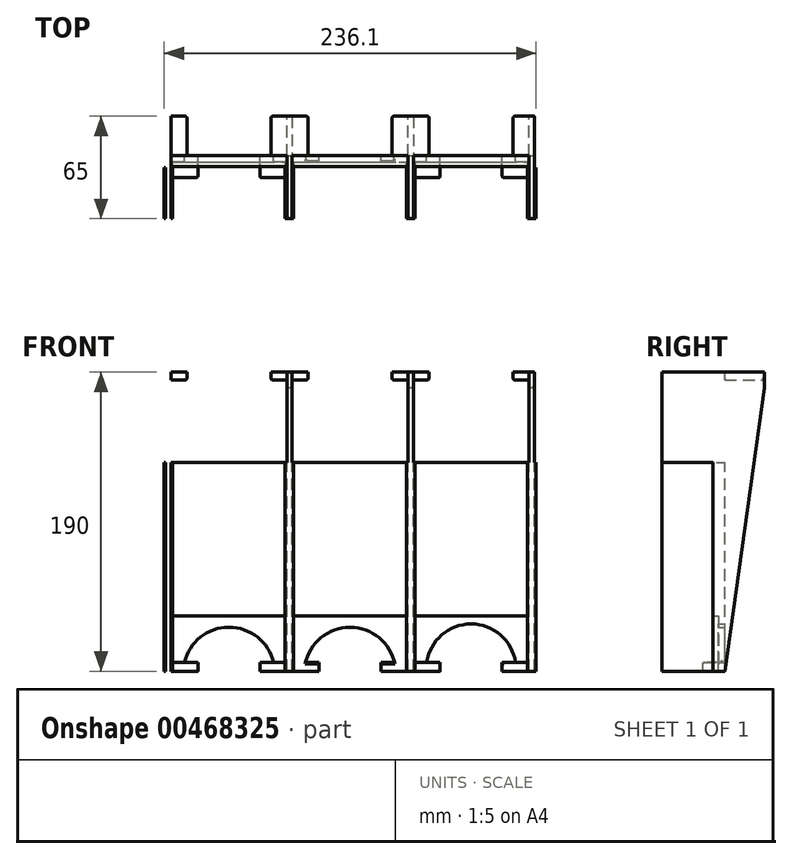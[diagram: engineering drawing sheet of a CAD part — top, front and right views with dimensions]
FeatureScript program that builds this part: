
annotation { "Feature Type Name" : "Feature", "Feature Type Description" : "" }
export const myFeature = defineFeature(function(context is Context, id is Id, definition is map)
    precondition{}
    {
        {
            var Q0;
            Q0=qCreatedBy(makeId("Top.planeOp"),FACE);
            var sketch = newSketch(context, id + "F0", { "sketchPlane" : qUnion([Q0])});
            skLineSegment(sketch, "E0.bottom", {"start": v(118.05, -35) * mm, "end": v(-118.05, -35) * mm});
            skLineSegment(sketch, "E0.top", {"start": v(118.05, 35) * mm, "end": v(-118.05, 35) * mm});
            skLineSegment(sketch, "E0.left", {"start": v(118.05, -35) * mm, "end": v(118.05, 35) * mm});
            skLineSegment(sketch, "E0.right", {"start": v(-118.05, -35) * mm, "end": v(-118.05, 35) * mm});
            skPoint(sketch, "E0.middle", {"position": v(0, 0) * mm});
            skLineSegment(sketch, "E1", {"start": v(-118.05, 30) * mm, "end": v(118.05, 30) * mm});
            skLineSegment(sketch, "E2", {"start": v(-112.65, -35) * mm, "end": v(-112.65, -2.5) * mm});
            skLineSegment(sketch, "E3", {"start": v(-112.65, -2.5) * mm, "end": v(-113.65, -2.5) * mm});
            skLineSegment(sketch, "E4", {"start": v(-113.65, -2.5) * mm, "end": v(-113.65, 30) * mm});
            skLineSegment(sketch, "E5", {"start": v(-41.15, -2.5) * mm, "end": v(-40.15, -2.5) * mm});
            skLineSegment(sketch, "E6", {"start": v(-40.15, -2.5) * mm, "end": v(-40.15, 30) * mm});
            skLineSegment(sketch, "E7", {"start": v(-41.15, -2.5) * mm, "end": v(-41.15, -35) * mm});
            skLineSegment(sketch, "E8", {"start": v(-36.75, 30) * mm, "end": v(-36.75, -2.5) * mm});
            skLineSegment(sketch, "E9", {"start": v(-36.75, -2.5) * mm, "end": v(-35.75, -2.5) * mm});
            skLineSegment(sketch, "E10", {"start": v(-35.75, -2.5) * mm, "end": v(-35.75, -35) * mm});
            skLineSegment(sketch, "E11", {"start": v(36.75, 30) * mm, "end": v(36.75, -2.5) * mm});
            skLineSegment(sketch, "E12", {"start": v(36.75, -2.5) * mm, "end": v(35.75, -2.5) * mm});
            skLineSegment(sketch, "E13", {"start": v(35.75, -2.5) * mm, "end": v(35.75, -35) * mm});
            skLineSegment(sketch, "E14", {"start": v(40.15, 30) * mm, "end": v(40.15, -2.5) * mm});
            skLineSegment(sketch, "E15", {"start": v(40.15, -2.5) * mm, "end": v(41.15, -2.5) * mm});
            skLineSegment(sketch, "E16", {"start": v(41.15, -2.5) * mm, "end": v(41.15, -35) * mm});
            skLineSegment(sketch, "E17", {"start": v(113.65, 30) * mm, "end": v(113.65, -2.5) * mm});
            skLineSegment(sketch, "E18", {"start": v(113.65, -2.5) * mm, "end": v(112.65, -2.5) * mm});
            skLineSegment(sketch, "E19", {"start": v(112.65, -2.5) * mm, "end": v(112.65, -35) * mm});
            skLineSegment(sketch, "E20", {"start": v(-113.65, -2) * mm, "end": v(-40.15, -2) * mm});
            skLineSegment(sketch, "E21", {"start": v(-36.75, -2) * mm, "end": v(36.75, -2) * mm});
            skLineSegment(sketch, "E22", {"start": v(40.15, -2) * mm, "end": v(113.65, -2) * mm});
            skLineSegment(sketch, "E23", {"start": v(-112.65, -2.5) * mm, "end": v(-112.65, -2) * mm});
            skLineSegment(sketch, "E24", {"start": v(-41.15, -2.5) * mm, "end": v(-41.15, -2) * mm});
            skLineSegment(sketch, "E25", {"start": v(-35.75, -2.5) * mm, "end": v(-35.75, -2) * mm});
            skLineSegment(sketch, "E26", {"start": v(35.75, -2.5) * mm, "end": v(35.75, -2) * mm});
            skLineSegment(sketch, "E27", {"start": v(41.15, -2.5) * mm, "end": v(41.15, -2) * mm});
            skLineSegment(sketch, "E28", {"start": v(112.65, -2.5) * mm, "end": v(112.65, -2) * mm});
            skLineSegment(sketch, "E29", {"start": v(-118.05, -2.5) * mm, "end": v(-117.05, -2.5) * mm});
            skLineSegment(sketch, "E30", {"start": v(-117.05, -2.5) * mm, "end": v(-117.05, 35) * mm});
            skLineSegment(sketch, "E31", {"start": v(118.05, -2.5) * mm, "end": v(117.05, -2.5) * mm});
            skLineSegment(sketch, "E32", {"start": v(117.05, -2.5) * mm, "end": v(117.05, 30) * mm});
            skLineSegment(sketch, "E33", {"start": v(-113.65, 5) * mm, "end": v(-103.65, 5) * mm});
            skLineSegment(sketch, "E34", {"start": v(-103.65, 5) * mm, "end": v(-103.65, 30) * mm});
            skLineSegment(sketch, "E35", {"start": v(-40.15, 5) * mm, "end": v(-50.15, 5) * mm});
            skLineSegment(sketch, "E36", {"start": v(-50.15, 5) * mm, "end": v(-50.15, 30) * mm});
            skLineSegment(sketch, "E37", {"start": v(-36.75, 5) * mm, "end": v(-26.75, 5) * mm});
            skLineSegment(sketch, "E38", {"start": v(-26.75, 5) * mm, "end": v(-26.75, 30) * mm});
            skLineSegment(sketch, "E39", {"start": v(36.75, 5) * mm, "end": v(26.75, 5) * mm});
            skLineSegment(sketch, "E40", {"start": v(26.75, 5) * mm, "end": v(26.75, 30) * mm});
            skLineSegment(sketch, "E41", {"start": v(40.15, 5) * mm, "end": v(50.15, 5) * mm});
            skLineSegment(sketch, "E42", {"start": v(50.15, 5) * mm, "end": v(50.15, 30) * mm});
            skLineSegment(sketch, "E43", {"start": v(113.65, 5) * mm, "end": v(103.65, 5) * mm});
            skLineSegment(sketch, "E44", {"start": v(103.65, 5) * mm, "end": v(103.65, 30) * mm});
            skLineSegment(sketch, "E45", {"start": v(117.05, 30) * mm, "end": v(117.05, 35) * mm});
            skLineSegment(sketch, "E46.bottom", {"start": v(-117.05, -2.5) * mm, "end": v(-113.65, -2.5) * mm, "construction": true});
            skLineSegment(sketch, "E46.top", {"start": v(-117.05, -35) * mm, "end": v(-113.65, -35) * mm});
            skLineSegment(sketch, "E46.left", {"start": v(-117.05, -2.5) * mm, "end": v(-117.05, -35) * mm});
            skLineSegment(sketch, "E46.right", {"start": v(-113.65, -2.5) * mm, "end": v(-113.65, -35) * mm});
            skLineSegment(sketch, "E47.bottom", {"start": v(-40.15, -2.5) * mm, "end": v(-36.75, -2.5) * mm, "construction": true});
            skLineSegment(sketch, "E47.top", {"start": v(-40.15, -35) * mm, "end": v(-36.75, -35) * mm, "construction": true});
            skLineSegment(sketch, "E47.left", {"start": v(-40.15, -2.5) * mm, "end": v(-40.15, -35) * mm});
            skLineSegment(sketch, "E47.right", {"start": v(-36.75, -2.5) * mm, "end": v(-36.75, -35) * mm});
            skLineSegment(sketch, "E48.bottom", {"start": v(36.75, -2.5) * mm, "end": v(40.15, -2.5) * mm});
            skLineSegment(sketch, "E48.top", {"start": v(36.75, -35) * mm, "end": v(40.15, -35) * mm});
            skLineSegment(sketch, "E48.left", {"start": v(36.75, -2.5) * mm, "end": v(36.75, -35) * mm});
            skLineSegment(sketch, "E48.right", {"start": v(40.15, -2.5) * mm, "end": v(40.15, -35) * mm});
            skLineSegment(sketch, "E49.bottom", {"start": v(113.65, -2.5) * mm, "end": v(117.05, -2.5) * mm});
            skLineSegment(sketch, "E49.top", {"start": v(113.65, -35) * mm, "end": v(117.05, -35) * mm});
            skLineSegment(sketch, "E49.left", {"start": v(113.65, -2.5) * mm, "end": v(113.65, -35) * mm});
            skLineSegment(sketch, "E49.right", {"start": v(117.05, -2.5) * mm, "end": v(117.05, -35) * mm});
            skLineSegment(sketch, "E50", {"start": v(-103.65, 5) * mm, "end": v(-50.15, 5) * mm});
            skLineSegment(sketch, "E51", {"start": v(-26.75, 5) * mm, "end": v(26.75, 5) * mm});
            skLineSegment(sketch, "E52", {"start": v(50.15, 5) * mm, "end": v(103.65, 5) * mm});
            skSolve(sketch);
        }
        {
            var Q0;
            {var subQ13=sQuery(id+"F0.wireOp",EDGE,"E5");Q0=makeQuery(id+"F0.imprint","IMPRINT",FACE,{"disambiguationData":[TD([[makeQuery(id+"F0.imprint","IMPRINT",EDGE,{"derivedFrom":subQ13}),-1.0]])]});}
            var Q1;
            {var subQ7=sQuery(id+"F0.wireOp",EDGE,"E12");Q1=makeQuery(id+"F0.imprint","IMPRINT",FACE,{"disambiguationData":[TD([[makeQuery(id+"F0.imprint","IMPRINT",EDGE,{"derivedFrom":subQ7}),1.0]])]});}
            var Q2;
            {var subQ0=sQuery(id+"F0.wireOp",EDGE,"E2");Q2=makeQuery(id+"F0.imprint","IMPRINT",FACE,{"disambiguationData":[TD([[makeQuery(id+"F0.imprint","IMPRINT",EDGE,{"derivedFrom":subQ0}),1.0]])]});}
            var Q3;
            {var subQ11=sQuery(id+"F0.wireOp",EDGE,"E18");Q3=makeQuery(id+"F0.imprint","IMPRINT",FACE,{"disambiguationData":[TD([[makeQuery(id+"F0.imprint","IMPRINT",EDGE,{"derivedFrom":subQ11}),1.0]])]});}
            var Q4;
            Q4=makeQuery(id+"F0.imprint","IMPRINT",FACE,{"disambiguationData":[TD([[makeQuery(id+"F0.imprint","IMPRINT",EDGE,{"derivedFrom":sQuery(id+"F0.wireOp",EDGE,"E48.bottom")}),-1.0]])]});
            var Q5;
            Q5=makeQuery(id+"F0.imprint","IMPRINT",FACE,{"disambiguationData":[TD([[makeQuery(id+"F0.imprint","IMPRINT",EDGE,{"derivedFrom":sQuery(id+"F0.wireOp",EDGE,"E15")}),-1.0]])]});
            var Q6;
            {var subQ0=sQuery(id+"F0.wireOp",EDGE,"E48.bottom");Q6=makeQuery(id+"F0.imprint","IMPRINT",FACE,{"disambiguationData":[TD([[makeQuery(id+"F0.imprint","IMPRINT",EDGE,{"derivedFrom":subQ0}),1.0]])]});}
            var Q7;
            Q7=makeQuery(id+"F0.imprint","IMPRINT",FACE,{"disambiguationData":[TD([[makeQuery(id+"F0.imprint","IMPRINT",EDGE,{"derivedFrom":sQuery(id+"F0.wireOp",EDGE,"E49.bottom")}),-1.0]])]});
            var Q8;
            {var subQ3=sQuery(id+"F0.wireOp",EDGE,"E32");Q8=makeQuery(id+"F0.imprint","IMPRINT",FACE,{"disambiguationData":[TD([[makeQuery(id+"F0.imprint","IMPRINT",EDGE,{"derivedFrom":subQ3}),1.0]])]});}
            var Q9;
            {var subQ4=sQuery(id+"F0.wireOp",EDGE,"E31");Q9=makeQuery(id+"F0.imprint","IMPRINT",FACE,{"disambiguationData":[TD([[makeQuery(id+"F0.imprint","IMPRINT",EDGE,{"derivedFrom":subQ4}),1.0]])]});}
            var Q10;
            Q10=makeQuery(id+"F0.imprint","IMPRINT",FACE,{"disambiguationData":[TD([[makeQuery(id+"F0.imprint","IMPRINT",EDGE,{"derivedFrom":sQuery(id+"F0.wireOp",EDGE,"E46.top")}),1.0]])]});
            var Q11;
            {var subQ4=sQuery(id+"F0.wireOp",EDGE,"E29");Q11=makeQuery(id+"F0.imprint","IMPRINT",FACE,{"disambiguationData":[TD([[makeQuery(id+"F0.imprint","IMPRINT",EDGE,{"derivedFrom":subQ4}),-1.0]])]});}
            var Q12;
            {var subQ9=sQuery(id+"F0.wireOp",EDGE,"E47.left");Q12=makeQuery(id+"F0.imprint","IMPRINT",FACE,{"disambiguationData":[TD([[makeQuery(id+"F0.imprint","IMPRINT",EDGE,{"derivedFrom":subQ9}),1.0]])]});}
            var Q13;
            Q13=makeQuery(id+"F0.imprint","IMPRINT",FACE,{"disambiguationData":[TD([[makeQuery(id+"F0.imprint","IMPRINT",EDGE,{"derivedFrom":sQuery(id+"F0.wireOp",EDGE,"E9")}),-1.0]])]});
            var Q14;
            {var subQ4=sQuery(id+"F0.wireOp",EDGE,"E37");Q14=makeQuery(id+"F0.imprint","IMPRINT",FACE,{"disambiguationData":[TD([[makeQuery(id+"F0.imprint","IMPRINT",EDGE,{"derivedFrom":subQ4}),-1.0]])]});}
            var Q15;
            {var subQ8=sQuery(id+"F0.wireOp",EDGE,"E33");Q15=makeQuery(id+"F0.imprint","IMPRINT",FACE,{"disambiguationData":[TD([[makeQuery(id+"F0.imprint","IMPRINT",EDGE,{"derivedFrom":subQ8}),-1.0]])]});}
            var Q16;
            {var subQ4=sQuery(id+"F0.wireOp",EDGE,"E41");Q16=makeQuery(id+"F0.imprint","IMPRINT",FACE,{"disambiguationData":[TD([[makeQuery(id+"F0.imprint","IMPRINT",EDGE,{"derivedFrom":subQ4}),-1.0]])]});}
            var Q17;
            {var subQ0=sQuery(id+"F0.wireOp",EDGE,"E3");Q17=makeQuery(id+"F0.imprint","IMPRINT",FACE,{"disambiguationData":[TD([[makeQuery(id+"F0.imprint","IMPRINT",EDGE,{"derivedFrom":subQ0}),-1.0]])]});}
            var Q18;
            {var subQ0=sQuery(id+"F0.wireOp",EDGE,"E5");Q18=makeQuery(id+"F0.imprint","IMPRINT",FACE,{"disambiguationData":[TD([[makeQuery(id+"F0.imprint","IMPRINT",EDGE,{"derivedFrom":subQ0}),1.0]])]});}
            var Q19;
            {var subQ0=sQuery(id+"F0.wireOp",EDGE,"E9");Q19=makeQuery(id+"F0.imprint","IMPRINT",FACE,{"disambiguationData":[TD([[makeQuery(id+"F0.imprint","IMPRINT",EDGE,{"derivedFrom":subQ0}),1.0]])]});}
            var Q20;
            {var subQ0=sQuery(id+"F0.wireOp",EDGE,"E12");Q20=makeQuery(id+"F0.imprint","IMPRINT",FACE,{"disambiguationData":[TD([[makeQuery(id+"F0.imprint","IMPRINT",EDGE,{"derivedFrom":subQ0}),-1.0]])]});}
            var Q21;
            {var subQ0=sQuery(id+"F0.wireOp",EDGE,"E15");Q21=makeQuery(id+"F0.imprint","IMPRINT",FACE,{"disambiguationData":[TD([[makeQuery(id+"F0.imprint","IMPRINT",EDGE,{"derivedFrom":subQ0}),1.0]])]});}
            var Q22;
            {var subQ0=sQuery(id+"F0.wireOp",EDGE,"E18");Q22=makeQuery(id+"F0.imprint","IMPRINT",FACE,{"disambiguationData":[TD([[makeQuery(id+"F0.imprint","IMPRINT",EDGE,{"derivedFrom":subQ0}),-1.0]])]});}
            extrude(context, id + "F1", {"entities" : qUnion([Q0, Q1, Q2, Q3, Q4, Q5, Q6, Q7, Q8, Q9, Q10, Q11, Q12, Q13, Q14, Q15, Q16, Q17, Q18, Q19, Q20, Q21, Q22]), "oppositeDirection" : true, "depth" : 190 * mm});
        }
        {
            var Q0;
            {var subQ4=sQuery(id+"F0.wireOp",EDGE,"E29");Q0=makeQuery(id+"F0.imprint","IMPRINT",FACE,{"disambiguationData":[TD([[makeQuery(id+"F0.imprint","IMPRINT",EDGE,{"derivedFrom":subQ4}),-1.0]])]});}
            var Q1;
            {var subQ0=sQuery(id+"F0.wireOp",EDGE,"E2");Q1=makeQuery(id+"F0.imprint","IMPRINT",FACE,{"disambiguationData":[TD([[makeQuery(id+"F0.imprint","IMPRINT",EDGE,{"derivedFrom":subQ0}),1.0]])]});}
            var Q2;
            Q2=makeQuery(id+"F0.imprint","IMPRINT",FACE,{"disambiguationData":[TD([[makeQuery(id+"F0.imprint","IMPRINT",EDGE,{"derivedFrom":sQuery(id+"F0.wireOp",EDGE,"E5")}),-1.0]])]});
            var Q3;
            Q3=makeQuery(id+"F0.imprint","IMPRINT",FACE,{"disambiguationData":[TD([[makeQuery(id+"F0.imprint","IMPRINT",EDGE,{"derivedFrom":sQuery(id+"F0.wireOp",EDGE,"E9")}),-1.0]])]});
            var Q4;
            Q4=makeQuery(id+"F0.imprint","IMPRINT",FACE,{"disambiguationData":[TD([[makeQuery(id+"F0.imprint","IMPRINT",EDGE,{"derivedFrom":sQuery(id+"F0.wireOp",EDGE,"E12")}),1.0]])]});
            var Q5;
            Q5=makeQuery(id+"F0.imprint","IMPRINT",FACE,{"disambiguationData":[TD([[makeQuery(id+"F0.imprint","IMPRINT",EDGE,{"derivedFrom":sQuery(id+"F0.wireOp",EDGE,"E15")}),-1.0]])]});
            var Q6;
            Q6=makeQuery(id+"F0.imprint","IMPRINT",FACE,{"disambiguationData":[TD([[makeQuery(id+"F0.imprint","IMPRINT",EDGE,{"derivedFrom":sQuery(id+"F0.wireOp",EDGE,"E18")}),1.0]])]});
            var Q7;
            {var subQ4=sQuery(id+"F0.wireOp",EDGE,"E31");Q7=makeQuery(id+"F0.imprint","IMPRINT",FACE,{"disambiguationData":[TD([[makeQuery(id+"F0.imprint","IMPRINT",EDGE,{"derivedFrom":subQ4}),1.0]])]});}
            var Q8;
            {var subQ0=sQuery(id+"F0.wireOp",EDGE,"E18");Q8=makeQuery(id+"F0.imprint","IMPRINT",FACE,{"disambiguationData":[TD([[makeQuery(id+"F0.imprint","IMPRINT",EDGE,{"derivedFrom":subQ0}),-1.0]])]});}
            var Q9;
            {var subQ0=sQuery(id+"F0.wireOp",EDGE,"E12");Q9=makeQuery(id+"F0.imprint","IMPRINT",FACE,{"disambiguationData":[TD([[makeQuery(id+"F0.imprint","IMPRINT",EDGE,{"derivedFrom":subQ0}),-1.0]])]});}
            var Q10;
            {var subQ0=sQuery(id+"F0.wireOp",EDGE,"E15");Q10=makeQuery(id+"F0.imprint","IMPRINT",FACE,{"disambiguationData":[TD([[makeQuery(id+"F0.imprint","IMPRINT",EDGE,{"derivedFrom":subQ0}),1.0]])]});}
            var Q11;
            {var subQ0=sQuery(id+"F0.wireOp",EDGE,"E9");Q11=makeQuery(id+"F0.imprint","IMPRINT",FACE,{"disambiguationData":[TD([[makeQuery(id+"F0.imprint","IMPRINT",EDGE,{"derivedFrom":subQ0}),1.0]])]});}
            var Q12;
            {var subQ0=sQuery(id+"F0.wireOp",EDGE,"E5");Q12=makeQuery(id+"F0.imprint","IMPRINT",FACE,{"disambiguationData":[TD([[makeQuery(id+"F0.imprint","IMPRINT",EDGE,{"derivedFrom":subQ0}),1.0]])]});}
            var Q13;
            {var subQ0=sQuery(id+"F0.wireOp",EDGE,"E3");Q13=makeQuery(id+"F0.imprint","IMPRINT",FACE,{"disambiguationData":[TD([[makeQuery(id+"F0.imprint","IMPRINT",EDGE,{"derivedFrom":subQ0}),-1.0]])]});}
            extrude(context, id + "F2", {"entities" : qUnion([Q0, Q1, Q2, Q3, Q4, Q5, Q6, Q7, Q8, Q9, Q10, Q11, Q12, Q13]), "operationType" : NewBodyOperationType.REMOVE, "oppositeDirection" : true, "depth" : 57.5 * mm});
        }
        {
            var Q0;
            {var subQ4=sQuery(id+"F0.wireOp",EDGE,"E43");Q0=makeQuery(id+"F0.imprint","IMPRINT",FACE,{"disambiguationData":[TD([[makeQuery(id+"F0.imprint","IMPRINT",EDGE,{"derivedFrom":subQ4}),-1.0]])]});}
            var Q1;
            {var subQ4=sQuery(id+"F0.wireOp",EDGE,"E39");Q1=makeQuery(id+"F0.imprint","IMPRINT",FACE,{"disambiguationData":[TD([[makeQuery(id+"F0.imprint","IMPRINT",EDGE,{"derivedFrom":subQ4}),-1.0]])]});}
            var Q2;
            {var subQ4=sQuery(id+"F0.wireOp",EDGE,"E35");Q2=makeQuery(id+"F0.imprint","IMPRINT",FACE,{"disambiguationData":[TD([[makeQuery(id+"F0.imprint","IMPRINT",EDGE,{"derivedFrom":subQ4}),-1.0]])]});}
            var Q3;
            {var subQ4=sQuery(id+"F0.wireOp",EDGE,"E33");Q3=makeQuery(id+"F0.imprint","IMPRINT",FACE,{"disambiguationData":[TD([[makeQuery(id+"F0.imprint","IMPRINT",EDGE,{"derivedFrom":subQ4}),1.0]])]});}
            var Q4;
            {var subQ4=sQuery(id+"F0.wireOp",EDGE,"E37");Q4=makeQuery(id+"F0.imprint","IMPRINT",FACE,{"disambiguationData":[TD([[makeQuery(id+"F0.imprint","IMPRINT",EDGE,{"derivedFrom":subQ4}),1.0]])]});}
            var Q5;
            {var subQ4=sQuery(id+"F0.wireOp",EDGE,"E41");Q5=makeQuery(id+"F0.imprint","IMPRINT",FACE,{"disambiguationData":[TD([[makeQuery(id+"F0.imprint","IMPRINT",EDGE,{"derivedFrom":subQ4}),1.0]])]});}
            extrude(context, id + "F3", {"entities" : qUnion([Q0, Q1, Q2, Q3, Q4, Q5]), "operationType" : NewBodyOperationType.ADD, "oppositeDirection" : true, "depth" : 5 * mm});
        }
        {
            var Q0;
            {var subQ8=sQuery(id+"F0.wireOp",EDGE,"E33");Q0=makeQuery(id+"F0.imprint","IMPRINT",FACE,{"disambiguationData":[TD([[makeQuery(id+"F0.imprint","IMPRINT",EDGE,{"derivedFrom":subQ8}),-1.0]])]});}
            var Q1;
            {var subQ4=sQuery(id+"F0.wireOp",EDGE,"E37");Q1=makeQuery(id+"F0.imprint","IMPRINT",FACE,{"disambiguationData":[TD([[makeQuery(id+"F0.imprint","IMPRINT",EDGE,{"derivedFrom":subQ4}),-1.0]])]});}
            var Q2;
            {var subQ4=sQuery(id+"F0.wireOp",EDGE,"E41");Q2=makeQuery(id+"F0.imprint","IMPRINT",FACE,{"disambiguationData":[TD([[makeQuery(id+"F0.imprint","IMPRINT",EDGE,{"derivedFrom":subQ4}),-1.0]])]});}
            extrude(context, id + "F4", {"entities" : qUnion([Q0, Q1, Q2]), "operationType" : NewBodyOperationType.REMOVE, "oppositeDirection" : true, "depth" : 57.5 * mm});
        }
        {
            var Q0;
            Q0=makeQuery(id+"F1.opExtrude","SWEPT_FACE",FACE,{"disambiguationData":[OSD([sQuery(id+"F0.wireOp",EDGE,"E37"),sQuery(id+"F0.wireOp",EDGE,"E39"),sQuery(id+"F0.wireOp",EDGE,"E51")])]});
            var sketch = newSketch(context, id + "F5", { "sketchPlane" : qUnion([Q0])});
            skLineSegment(sketch, "E53.bottom", {"start": v(-113.65, -184.5) * mm, "end": v(-96.65, -184.5) * mm});
            skLineSegment(sketch, "E53.top", {"start": v(-113.65, -190) * mm, "end": v(-96.65, -190) * mm});
            skLineSegment(sketch, "E53.left", {"start": v(-113.65, -184.5) * mm, "end": v(-113.65, -190) * mm});
            skLineSegment(sketch, "E53.right", {"start": v(-96.65, -184.5) * mm, "end": v(-96.65, -190) * mm});
            skLineSegment(sketch, "E54.bottom", {"start": v(-57.15, -184.5) * mm, "end": v(-40.15, -184.5) * mm});
            skLineSegment(sketch, "E54.top", {"start": v(-57.15, -190) * mm, "end": v(-40.15, -190) * mm});
            skLineSegment(sketch, "E54.left", {"start": v(-57.15, -184.5) * mm, "end": v(-57.15, -190) * mm});
            skLineSegment(sketch, "E54.right", {"start": v(-40.15, -184.5) * mm, "end": v(-40.15, -190) * mm});
            skLineSegment(sketch, "E55.bottom", {"start": v(-36.75, -190) * mm, "end": v(-19.75, -190) * mm});
            skLineSegment(sketch, "E55.top", {"start": v(-36.75, -184.5) * mm, "end": v(-19.75, -184.5) * mm});
            skLineSegment(sketch, "E55.left", {"start": v(-36.75, -190) * mm, "end": v(-36.75, -184.5) * mm});
            skLineSegment(sketch, "E55.right", {"start": v(-19.75, -190) * mm, "end": v(-19.75, -184.5) * mm});
            skLineSegment(sketch, "E56.bottom", {"start": v(19.75, -190) * mm, "end": v(36.75, -190) * mm});
            skLineSegment(sketch, "E56.top", {"start": v(19.75, -184.5) * mm, "end": v(36.75, -184.5) * mm});
            skLineSegment(sketch, "E56.left", {"start": v(19.75, -190) * mm, "end": v(19.75, -184.5) * mm});
            skLineSegment(sketch, "E56.right", {"start": v(36.75, -190) * mm, "end": v(36.75, -184.5) * mm});
            skLineSegment(sketch, "E57.bottom", {"start": v(40.15, -190) * mm, "end": v(57.15, -190) * mm});
            skLineSegment(sketch, "E57.top", {"start": v(40.15, -184.5) * mm, "end": v(57.15, -184.5) * mm});
            skLineSegment(sketch, "E57.left", {"start": v(40.15, -190) * mm, "end": v(40.15, -184.5) * mm});
            skLineSegment(sketch, "E57.right", {"start": v(57.15, -190) * mm, "end": v(57.15, -184.5) * mm});
            skLineSegment(sketch, "E58.bottom", {"start": v(96.65, -190) * mm, "end": v(113.65, -190) * mm});
            skLineSegment(sketch, "E58.top", {"start": v(96.65, -184.5) * mm, "end": v(113.65, -184.5) * mm});
            skLineSegment(sketch, "E58.left", {"start": v(96.65, -190) * mm, "end": v(96.65, -184.5) * mm});
            skLineSegment(sketch, "E58.right", {"start": v(113.65, -190) * mm, "end": v(113.65, -184.5) * mm});
            skArc(sketch, "E59", {"start": v(28.25, -184.5) * mm, "mid": v(0, -162.02) * mm, "end": v(-28.25, -184.5) * mm});
            skSolve(sketch);
        }
        {
            var Q0;
            {var subQ0=sQuery(id+"F0.wireOp",EDGE,"E1");Q0=makeQuery(id+"F1.opExtrude","CAP_EDGE",EDGE,{"disambiguationData":[OSD([subQ0]),TDD([makeQuery(id+"F0.imprint","IMPRINT",EDGE,{"disambiguationData":[TD([[makeQuery(id+"F0.imprint","INTERSECT",VERTEX,{"derivedFrom":[subQ0,sQuery(id+"F0.wireOp",EDGE,"E17")]}),-1.0]])],"derivedFrom":subQ0})])],"isStart":false});}
            var Q1;
            {var subQ0=sQuery(id+"F0.wireOp",EDGE,"E1");Q1=makeQuery(id+"F1.opExtrude","CAP_EDGE",EDGE,{"disambiguationData":[OSD([subQ0]),TDD([makeQuery(id+"F0.imprint","IMPRINT",EDGE,{"disambiguationData":[TD([[makeQuery(id+"F0.imprint","INTERSECT",VERTEX,{"derivedFrom":[subQ0,sQuery(id+"F0.wireOp",EDGE,"E11")]}),-1.0]])],"derivedFrom":subQ0})])],"isStart":false});}
            var Q2;
            {var subQ0=sQuery(id+"F0.wireOp",EDGE,"E1");Q2=makeQuery(id+"F1.opExtrude","CAP_EDGE",EDGE,{"disambiguationData":[OSD([subQ0]),TDD([makeQuery(id+"F0.imprint","IMPRINT",EDGE,{"disambiguationData":[TD([[makeQuery(id+"F0.imprint","INTERSECT",VERTEX,{"derivedFrom":[subQ0,sQuery(id+"F0.wireOp",EDGE,"E6")]}),-1.0]])],"derivedFrom":subQ0})])],"isStart":false});}
            var Q3;
            {var subQ0=sQuery(id+"F0.wireOp",EDGE,"E1");Q3=makeQuery(id+"F1.opExtrude","CAP_EDGE",EDGE,{"disambiguationData":[OSD([subQ0]),TDD([makeQuery(id+"F0.imprint","IMPRINT",EDGE,{"disambiguationData":[TD([[makeQuery(id+"F0.imprint","INTERSECT",VERTEX,{"derivedFrom":[subQ0,sQuery(id+"F0.wireOp",EDGE,"E4")]}),1.0]])],"derivedFrom":subQ0})])],"isStart":false});}
            chamfer(context, id + "F6", {"entities" : qUnion([Q0, Q1, Q2, Q3]), "chamferType" : ChamferType.TWO_OFFSETS, "width1" : 25 * mm, "oppositeDirection" : false, "width2" : 180 * mm, "tangentPropagation" : true});
        }
        {
            var Q0;
            Q0=makeQuery(id+"F1.opExtrude","CAP_FACE",FACE,{"disambiguationData":[OSD([sQuery(id+"F0.wireOp",EDGE,"E0.bottom"),sQuery(id+"F0.wireOp",EDGE,"E0.left"),sQuery(id+"F0.wireOp",EDGE,"E0.right"),sQuery(id+"F0.wireOp",EDGE,"E1"),sQuery(id+"F0.wireOp",EDGE,"E2"),sQuery(id+"F0.wireOp",EDGE,"E4"),sQuery(id+"F0.wireOp",EDGE,"E6"),sQuery(id+"F0.wireOp",EDGE,"E7"),sQuery(id+"F0.wireOp",EDGE,"E8"),sQuery(id+"F0.wireOp",EDGE,"E10"),sQuery(id+"F0.wireOp",EDGE,"E11"),sQuery(id+"F0.wireOp",EDGE,"E13"),sQuery(id+"F0.wireOp",EDGE,"E14"),sQuery(id+"F0.wireOp",EDGE,"E16"),sQuery(id+"F0.wireOp",EDGE,"E17"),sQuery(id+"F0.wireOp",EDGE,"E19"),sQuery(id+"F0.wireOp",EDGE,"E20"),sQuery(id+"F0.wireOp",EDGE,"E21"),sQuery(id+"F0.wireOp",EDGE,"E22"),sQuery(id+"F0.wireOp",EDGE,"E23"),sQuery(id+"F0.wireOp",EDGE,"E24"),sQuery(id+"F0.wireOp",EDGE,"E25"),sQuery(id+"F0.wireOp",EDGE,"E26"),sQuery(id+"F0.wireOp",EDGE,"E27"),sQuery(id+"F0.wireOp",EDGE,"E28"),sQuery(id+"F0.wireOp",EDGE,"E29"),sQuery(id+"F0.wireOp",EDGE,"E30"),sQuery(id+"F0.wireOp",EDGE,"E31"),sQuery(id+"F0.wireOp",EDGE,"E32"),sQuery(id+"F0.wireOp",EDGE,"E33"),sQuery(id+"F0.wireOp",EDGE,"E35"),sQuery(id+"F0.wireOp",EDGE,"E37"),sQuery(id+"F0.wireOp",EDGE,"E39"),sQuery(id+"F0.wireOp",EDGE,"E41"),sQuery(id+"F0.wireOp",EDGE,"E43"),sQuery(id+"F0.wireOp",EDGE,"E46.top"),sQuery(id+"F0.wireOp",EDGE,"E48.top"),sQuery(id+"F0.wireOp",EDGE,"E49.top"),sQuery(id+"F0.wireOp",EDGE,"E50"),sQuery(id+"F0.wireOp",EDGE,"E51"),sQuery(id+"F0.wireOp",EDGE,"E52")])],"isStart":false});
            var sketch = newSketch(context, id + "F7", { "sketchPlane" : qUnion([Q0])});
            skLineSegment(sketch, "E60.bottom", {"start": v(-112.65, 2) * mm, "end": v(-41.15, 2) * mm});
            skLineSegment(sketch, "E60.top", {"start": v(-112.65, -1) * mm, "end": v(-41.15, -1) * mm});
            skLineSegment(sketch, "E60.left", {"start": v(-112.65, 2) * mm, "end": v(-112.65, -1) * mm});
            skLineSegment(sketch, "E60.right", {"start": v(-41.15, 2) * mm, "end": v(-41.15, -1) * mm});
            skLineSegment(sketch, "E61.bottom", {"start": v(-35.75, 2) * mm, "end": v(35.75, 2) * mm});
            skLineSegment(sketch, "E61.top", {"start": v(-35.75, -1) * mm, "end": v(35.75, -1) * mm});
            skLineSegment(sketch, "E61.left", {"start": v(-35.75, 2) * mm, "end": v(-35.75, -1) * mm});
            skLineSegment(sketch, "E61.right", {"start": v(35.75, 2) * mm, "end": v(35.75, -1) * mm});
            skLineSegment(sketch, "E62.bottom", {"start": v(41.15, 2) * mm, "end": v(112.65, 2) * mm});
            skLineSegment(sketch, "E62.top", {"start": v(41.15, -1) * mm, "end": v(112.65, -1) * mm});
            skLineSegment(sketch, "E62.left", {"start": v(41.15, 2) * mm, "end": v(41.15, -1) * mm});
            skLineSegment(sketch, "E62.right", {"start": v(112.65, 2) * mm, "end": v(112.65, -1) * mm});
            skSolve(sketch);
        }
        {
            var Q0;
            Q0=makeQuery(id+"F7.imprint","IMPRINT",FACE,{"disambiguationData":[TD([[makeQuery(id+"F7.imprint","IMPRINT",EDGE,{"derivedFrom":sQuery(id+"F7.wireOp",EDGE,"E62.bottom")}),-1.0]])]});
            var Q1;
            Q1=makeQuery(id+"F7.imprint","IMPRINT",FACE,{"disambiguationData":[TD([[makeQuery(id+"F7.imprint","IMPRINT",EDGE,{"derivedFrom":sQuery(id+"F7.wireOp",EDGE,"E61.bottom")}),-1.0]])]});
            var Q2;
            Q2=makeQuery(id+"F7.imprint","IMPRINT",FACE,{"disambiguationData":[TD([[makeQuery(id+"F7.imprint","IMPRINT",EDGE,{"derivedFrom":sQuery(id+"F7.wireOp",EDGE,"E60.bottom")}),-1.0]])]});
            extrude(context, id + "F8", {"entities" : qUnion([Q0, Q1, Q2]), "operationType" : NewBodyOperationType.REMOVE, "oppositeDirection" : true, "depth" : 35 * mm});
        }
        {
            var Q0;
            {var subQ1=sQuery(id+"F5.wireOp",EDGE,"E55.right");Q0=makeQuery(id+"F5.imprint","IMPRINT",FACE,{"disambiguationData":[TD([[makeQuery(id+"F5.imprint","IMPRINT",EDGE,{"derivedFrom":subQ1}),-1.0]])]});}
            var Q1;
            Q1=makeQuery(id+"F5.imprint","IMPRINT",FACE,{"disambiguationData":[TD([[makeQuery(id+"F5.imprint","IMPRINT",EDGE,{"derivedFrom":sQuery(id+"F5.wireOp",EDGE,"E54.bottom")}),-1.0]])]});
            var Q2;
            Q2=makeQuery(id+"F5.imprint","IMPRINT",FACE,{"disambiguationData":[TD([[makeQuery(id+"F5.imprint","IMPRINT",EDGE,{"derivedFrom":sQuery(id+"F5.wireOp",EDGE,"E53.bottom")}),-1.0]])]});
            var Q3;
            Q3=makeQuery(id+"F5.imprint","IMPRINT",FACE,{"disambiguationData":[TD([[makeQuery(id+"F5.imprint","IMPRINT",EDGE,{"derivedFrom":sQuery(id+"F5.wireOp",EDGE,"E57.bottom")}),1.0]])]});
            var Q4;
            Q4=makeQuery(id+"F5.imprint","IMPRINT",FACE,{"disambiguationData":[TD([[makeQuery(id+"F5.imprint","IMPRINT",EDGE,{"derivedFrom":sQuery(id+"F5.wireOp",EDGE,"E58.bottom")}),1.0]])]});
            var Q5;
            Q5=makeQuery(id+"F5.imprint","IMPRINT",FACE,{"disambiguationData":[TD([[makeQuery(id+"F5.imprint","IMPRINT",EDGE,{"derivedFrom":sQuery(id+"F5.wireOp",EDGE,"E55.bottom")}),-1.0]])]});
            var Q6;
            Q6=makeQuery(id+"F5.imprint","IMPRINT",FACE,{"disambiguationData":[TD([[makeQuery(id+"F5.imprint","IMPRINT",EDGE,{"derivedFrom":sQuery(id+"F5.wireOp",EDGE,"E56.bottom")}),-1.0]])]});
            extrude(context, id + "F9", {"entities" : qUnion([Q0, Q1, Q2, Q3, Q4, Q5, Q6]), "operationType" : NewBodyOperationType.REMOVE, "oppositeDirection" : true, "depth" : 25 * mm});
        }
        {
            var Q0;
            Q0=makeQuery(id+"F1.opExtrude","SWEPT_FACE",FACE,{"disambiguationData":[OSD([sQuery(id+"F0.wireOp",EDGE,"E41"),sQuery(id+"F0.wireOp",EDGE,"E43"),sQuery(id+"F0.wireOp",EDGE,"E52")])]});
            var sketch = newSketch(context, id + "F10", { "sketchPlane" : qUnion([Q0])});
            skArc(sketch, "E63", {"start": v(-48.65, -184.5) * mm, "mid": v(-76.9, -160) * mm, "end": v(-105.15, -184.5) * mm});
            skSolve(sketch);
        }
        {
            var Q0;
            Q0=makeQuery(id+"F1.opExtrude","SWEPT_FACE",FACE,{"disambiguationData":[OSD([sQuery(id+"F0.wireOp",EDGE,"E33"),sQuery(id+"F0.wireOp",EDGE,"E35"),sQuery(id+"F0.wireOp",EDGE,"E50")])]});
            var sketch = newSketch(context, id + "F11", { "sketchPlane" : qUnion([Q0])});
            skArc(sketch, "E64", {"start": v(105.15, -184.5) * mm, "mid": v(76.9, -162.02) * mm, "end": v(48.65, -184.5) * mm});
            skSolve(sketch);
        }
        {
            var Q0;
            Q0=makeQuery(id+"F11.imprint","IMPRINT",FACE,{"disambiguationData":[TD([[makeQuery(id+"F11.imprint","IMPRINT",EDGE,{"derivedFrom":sQuery(id+"F11.wireOp",EDGE,"T8UIEtZj-yiWf-eJ33-j3sv-H2AG15FXrbVh")}),1.0]])]});
            var Q1;
            {var subQ2=sQuery(id+"F11.wireOp",EDGE,"E64");Q1=makeQuery(id+"F11.imprint","IMPRINT",FACE,{"disambiguationData":[TD([[makeQuery(id+"F11.imprint","IMPRINT",EDGE,{"derivedFrom":subQ2}),1.0]])]});}
            var Q2;
            {var subQ2=sQuery(id+"F10.wireOp",EDGE,"E63");Q2=makeQuery(id+"F10.imprint","IMPRINT",FACE,{"disambiguationData":[TD([[makeQuery(id+"F10.imprint","IMPRINT",EDGE,{"derivedFrom":subQ2}),1.0]])]});}
            extrude(context, id + "F12", {"entities" : qUnion([Q0, Q1, Q2]), "operationType" : NewBodyOperationType.REMOVE, "oppositeDirection" : true, "depth" : 25 * mm});
        }
        {
            var Q0;
            Q0=makeQuery(id+"F5.imprint","IMPRINT",FACE,{"disambiguationData":[TD([[makeQuery(id+"F5.imprint","IMPRINT",EDGE,{"derivedFrom":sQuery(id+"F5.wireOp",EDGE,"E53.bottom")}),-1.0]])]});
            var Q1;
            Q1=makeQuery(id+"F5.imprint","IMPRINT",FACE,{"disambiguationData":[TD([[makeQuery(id+"F5.imprint","IMPRINT",EDGE,{"derivedFrom":sQuery(id+"F5.wireOp",EDGE,"E54.bottom")}),-1.0]])]});
            var Q2;
            Q2=makeQuery(id+"F5.imprint","IMPRINT",FACE,{"disambiguationData":[TD([[makeQuery(id+"F5.imprint","IMPRINT",EDGE,{"derivedFrom":sQuery(id+"F5.wireOp",EDGE,"E55.bottom")}),-1.0]])]});
            var Q3;
            Q3=makeQuery(id+"F5.imprint","IMPRINT",FACE,{"disambiguationData":[TD([[makeQuery(id+"F5.imprint","IMPRINT",EDGE,{"derivedFrom":sQuery(id+"F5.wireOp",EDGE,"E56.bottom")}),-1.0]])]});
            var Q4;
            Q4=makeQuery(id+"F5.imprint","IMPRINT",FACE,{"disambiguationData":[TD([[makeQuery(id+"F5.imprint","IMPRINT",EDGE,{"derivedFrom":sQuery(id+"F5.wireOp",EDGE,"E57.bottom")}),1.0]])]});
            var Q5;
            Q5=makeQuery(id+"F5.imprint","IMPRINT",FACE,{"disambiguationData":[TD([[makeQuery(id+"F5.imprint","IMPRINT",EDGE,{"derivedFrom":sQuery(id+"F5.wireOp",EDGE,"E58.bottom")}),1.0]])]});
            extrude(context, id + "F13", {"entities" : qUnion([Q0, Q1, Q2, Q3, Q4, Q5]), "operationType" : NewBodyOperationType.ADD, "oppositeDirection" : true, "depth" : 14 * mm});
        }
        {
            var Q0;
            Q0=makeQuery(id+"F9.boolean.opBoolean","COPY",FACE,{"derivedFrom":makeQuery(id+"F9.opExtrude","CAP_FACE",FACE,{"disambiguationData":[OSD([sQuery(id+"F5.wireOp",EDGE,"E53.bottom"),sQuery(id+"F5.wireOp",EDGE,"E53.top"),sQuery(id+"F5.wireOp",EDGE,"E53.left"),sQuery(id+"F5.wireOp",EDGE,"E53.right")])],"isStart":false})});
            var Q1;
            Q1=makeQuery(id+"F9.boolean.opBoolean","COPY",FACE,{"derivedFrom":makeQuery(id+"F9.opExtrude","CAP_FACE",FACE,{"disambiguationData":[OSD([sQuery(id+"F5.wireOp",EDGE,"E54.bottom"),sQuery(id+"F5.wireOp",EDGE,"E54.top"),sQuery(id+"F5.wireOp",EDGE,"E54.left"),sQuery(id+"F5.wireOp",EDGE,"E54.right")])],"isStart":false})});
            var Q2;
            {var subQ2=sQuery(id+"F0.wireOp",EDGE,"E11");var subQ3=sQuery(id+"F0.wireOp",EDGE,"E51");var subQ4=sQuery(id+"F0.wireOp",EDGE,"E39");var subQ5=sQuery(id+"F0.wireOp",EDGE,"E37");var subQ6=sQuery(id+"F5.wireOp",EDGE,"E55.top");var subQ7=sQuery(id+"F5.wireOp",EDGE,"E55.left");Q2=makeQuery(id+"F9.boolean.opBoolean","COPY",FACE,{"disambiguationData":[TD([makeQuery(id+"F1.opExtrude","SWEPT_FACE",FACE,{"disambiguationData":[OSD([subQ2])]})])],"derivedFrom":makeQuery(id+"F9.opExtrude","CAP_FACE",FACE,{"disambiguationData":[OSD([subQ5,subQ4,subQ3,sQuery(id+"F5.wireOp",EDGE,"E55.bottom"),subQ6,subQ7,sQuery(id+"F5.wireOp",EDGE,"E56.bottom"),sQuery(id+"F5.wireOp",EDGE,"E56.top"),sQuery(id+"F5.wireOp",EDGE,"E56.right"),sQuery(id+"F5.wireOp",EDGE,"E59")])],"isStart":false})});}
            var Q3;
            Q3=makeQuery(id+"F9.boolean.opBoolean","COPY",FACE,{"derivedFrom":makeQuery(id+"F9.opExtrude","CAP_FACE",FACE,{"disambiguationData":[OSD([sQuery(id+"F5.wireOp",EDGE,"E57.bottom"),sQuery(id+"F5.wireOp",EDGE,"E57.top"),sQuery(id+"F5.wireOp",EDGE,"E57.left"),sQuery(id+"F5.wireOp",EDGE,"E57.right")])],"isStart":false})});
            var Q4;
            {var subQ0=sQuery(id+"F0.wireOp",EDGE,"E8");var subQ1=sQuery(id+"F0.wireOp",EDGE,"E51");var subQ2=sQuery(id+"F0.wireOp",EDGE,"E39");var subQ3=sQuery(id+"F0.wireOp",EDGE,"E37");var subQ6=sQuery(id+"F5.wireOp",EDGE,"E56.top");var subQ7=sQuery(id+"F5.wireOp",EDGE,"E56.right");Q4=makeQuery(id+"F9.boolean.opBoolean","COPY",FACE,{"disambiguationData":[TD([makeQuery(id+"F1.opExtrude","SWEPT_FACE",FACE,{"disambiguationData":[OSD([subQ0])]})])],"derivedFrom":makeQuery(id+"F9.opExtrude","CAP_FACE",FACE,{"disambiguationData":[OSD([subQ3,subQ2,subQ1,sQuery(id+"F5.wireOp",EDGE,"E55.bottom"),sQuery(id+"F5.wireOp",EDGE,"E55.top"),sQuery(id+"F5.wireOp",EDGE,"E55.left"),sQuery(id+"F5.wireOp",EDGE,"E56.bottom"),subQ6,subQ7,sQuery(id+"F5.wireOp",EDGE,"E59")])],"isStart":false})});}
            var Q5;
            Q5=makeQuery(id+"F9.boolean.opBoolean","COPY",FACE,{"derivedFrom":makeQuery(id+"F9.opExtrude","CAP_FACE",FACE,{"disambiguationData":[OSD([sQuery(id+"F5.wireOp",EDGE,"E58.bottom"),sQuery(id+"F5.wireOp",EDGE,"E58.top"),sQuery(id+"F5.wireOp",EDGE,"E58.left"),sQuery(id+"F5.wireOp",EDGE,"E58.right")])],"isStart":false})});
            var Q6;
            Q6=makeQuery(id+"F13.opExtrude","CAP_FACE",FACE,{"disambiguationData":[OSD([sQuery(id+"F5.wireOp",EDGE,"E53.bottom"),sQuery(id+"F5.wireOp",EDGE,"E53.top"),sQuery(id+"F5.wireOp",EDGE,"E53.left"),sQuery(id+"F5.wireOp",EDGE,"E53.right")])],"isStart":false});
            extrude(context, id + "F14", {"entities" : qUnion([Q0, Q1, Q2, Q3, Q4, Q5]), "operationType" : NewBodyOperationType.ADD, "endBound" : BoundingType.UP_TO_SURFACE, "endBoundEntityFace" : qUnion([Q6]), "depth" : 25 * mm});
        }
        {
            var Q0;
            {var subQ0=makeQuery(id+"F1.opExtrude","SWEPT_FACE",FACE,{"disambiguationData":[OSD([sQuery(id+"F0.wireOp",EDGE,"E19"),sQuery(id+"F0.wireOp",EDGE,"E28")])]});var subQ1=makeQuery(id+"F8.opExtrude","SWEPT_FACE",FACE,{"disambiguationData":[OSD([sQuery(id+"F7.wireOp",EDGE,"E62.right")])]});var subQ2=sQuery(id+"F5.wireOp",EDGE,"E53.bottom");Q0=makeQuery(id+"F13.boolean.opBoolean","SPLIT",EDGE,{"disambiguationData":[topologyDisambiguationEdgeConnected([makeQuery(id+"F13.opExtrude","SWEPT_FACE",FACE,{"disambiguationData":[OSD([subQ2])]})])],"derivedFrom":makeQuery(id+"F9.boolean.opBoolean","INTERSECT",EDGE,{"derivedFrom":[makeQuery(id+"F8.boolean.opBoolean","MERGE",FACE,{"derivedFrom":[subQ0,subQ1]}),makeQuery(id+"F9.opExtrude","SWEPT_FACE",FACE,{"disambiguationData":[OSD([subQ2])]})]})});}
            var Q1;
            Q1=makeQuery(id+"F9.boolean.opBoolean","INTERSECT",EDGE,{"derivedFrom":[makeQuery(id+"F8.boolean.opBoolean","COPY",FACE,{"derivedFrom":makeQuery(id+"F8.opExtrude","SWEPT_FACE",FACE,{"disambiguationData":[OSD([sQuery(id+"F7.wireOp",EDGE,"E62.top")])]})}),makeQuery(id+"F9.opExtrude","SWEPT_FACE",FACE,{"disambiguationData":[OSD([sQuery(id+"F5.wireOp",EDGE,"E53.bottom")])]})]});
            var Q2;
            Q2=makeQuery(id+"F9.boolean.opBoolean","INTERSECT",EDGE,{"derivedFrom":[makeQuery(id+"F8.boolean.opBoolean","COPY",FACE,{"derivedFrom":makeQuery(id+"F8.opExtrude","SWEPT_FACE",FACE,{"disambiguationData":[OSD([sQuery(id+"F7.wireOp",EDGE,"E62.top")])]})}),makeQuery(id+"F9.opExtrude","SWEPT_FACE",FACE,{"disambiguationData":[OSD([sQuery(id+"F5.wireOp",EDGE,"E54.bottom")])]})]});
            var Q3;
            {var subQ0=makeQuery(id+"F1.opExtrude","SWEPT_FACE",FACE,{"disambiguationData":[OSD([sQuery(id+"F0.wireOp",EDGE,"E16"),sQuery(id+"F0.wireOp",EDGE,"E27")])]});var subQ1=makeQuery(id+"F8.opExtrude","SWEPT_FACE",FACE,{"disambiguationData":[OSD([sQuery(id+"F7.wireOp",EDGE,"E62.left")])]});var subQ2=sQuery(id+"F5.wireOp",EDGE,"E54.bottom");Q3=makeQuery(id+"F13.boolean.opBoolean","SPLIT",EDGE,{"disambiguationData":[topologyDisambiguationEdgeConnected([makeQuery(id+"F13.opExtrude","SWEPT_FACE",FACE,{"disambiguationData":[OSD([subQ2])]})])],"derivedFrom":makeQuery(id+"F9.boolean.opBoolean","INTERSECT",EDGE,{"derivedFrom":[makeQuery(id+"F8.boolean.opBoolean","MERGE",FACE,{"derivedFrom":[subQ0,subQ1]}),makeQuery(id+"F9.opExtrude","SWEPT_FACE",FACE,{"disambiguationData":[OSD([subQ2])]})]})});}
            var Q4;
            Q4=makeQuery(id+"F9.boolean.opBoolean","INTERSECT",EDGE,{"derivedFrom":[makeQuery(id+"F8.boolean.opBoolean","COPY",FACE,{"derivedFrom":makeQuery(id+"F8.opExtrude","SWEPT_FACE",FACE,{"disambiguationData":[OSD([sQuery(id+"F7.wireOp",EDGE,"E61.top")])]})}),makeQuery(id+"F9.opExtrude","SWEPT_FACE",FACE,{"disambiguationData":[OSD([sQuery(id+"F5.wireOp",EDGE,"E55.top")])]})]});
            var Q5;
            {var subQ0=makeQuery(id+"F1.opExtrude","SWEPT_FACE",FACE,{"disambiguationData":[OSD([sQuery(id+"F0.wireOp",EDGE,"E13"),sQuery(id+"F0.wireOp",EDGE,"E26")])]});var subQ1=makeQuery(id+"F8.opExtrude","SWEPT_FACE",FACE,{"disambiguationData":[OSD([sQuery(id+"F7.wireOp",EDGE,"E61.right")])]});var subQ2=sQuery(id+"F5.wireOp",EDGE,"E55.top");Q5=makeQuery(id+"F13.boolean.opBoolean","SPLIT",EDGE,{"disambiguationData":[topologyDisambiguationEdgeConnected([makeQuery(id+"F13.opExtrude","SWEPT_FACE",FACE,{"disambiguationData":[OSD([subQ2])]})])],"derivedFrom":makeQuery(id+"F9.boolean.opBoolean","INTERSECT",EDGE,{"derivedFrom":[makeQuery(id+"F8.boolean.opBoolean","MERGE",FACE,{"derivedFrom":[subQ0,subQ1]}),makeQuery(id+"F9.opExtrude","SWEPT_FACE",FACE,{"disambiguationData":[OSD([subQ2])]})]})});}
            var Q6;
            Q6=makeQuery(id+"F9.boolean.opBoolean","INTERSECT",EDGE,{"derivedFrom":[makeQuery(id+"F8.boolean.opBoolean","COPY",FACE,{"derivedFrom":makeQuery(id+"F8.opExtrude","SWEPT_FACE",FACE,{"disambiguationData":[OSD([sQuery(id+"F7.wireOp",EDGE,"E61.top")])]})}),makeQuery(id+"F9.opExtrude","SWEPT_FACE",FACE,{"disambiguationData":[OSD([sQuery(id+"F5.wireOp",EDGE,"E56.top")])]})]});
            var Q7;
            {var subQ0=makeQuery(id+"F1.opExtrude","SWEPT_FACE",FACE,{"disambiguationData":[OSD([sQuery(id+"F0.wireOp",EDGE,"E10"),sQuery(id+"F0.wireOp",EDGE,"E25")])]});var subQ1=makeQuery(id+"F8.opExtrude","SWEPT_FACE",FACE,{"disambiguationData":[OSD([sQuery(id+"F7.wireOp",EDGE,"E61.left")])]});var subQ2=sQuery(id+"F5.wireOp",EDGE,"E56.top");Q7=makeQuery(id+"F13.boolean.opBoolean","SPLIT",EDGE,{"disambiguationData":[topologyDisambiguationEdgeConnected([makeQuery(id+"F13.opExtrude","SWEPT_FACE",FACE,{"disambiguationData":[OSD([subQ2])]})])],"derivedFrom":makeQuery(id+"F9.boolean.opBoolean","INTERSECT",EDGE,{"derivedFrom":[makeQuery(id+"F8.boolean.opBoolean","MERGE",FACE,{"derivedFrom":[subQ0,subQ1]}),makeQuery(id+"F9.opExtrude","SWEPT_FACE",FACE,{"disambiguationData":[OSD([subQ2])]})]})});}
            var Q8;
            {var subQ0=makeQuery(id+"F1.opExtrude","SWEPT_FACE",FACE,{"disambiguationData":[OSD([sQuery(id+"F0.wireOp",EDGE,"E7"),sQuery(id+"F0.wireOp",EDGE,"E24")])]});var subQ1=makeQuery(id+"F8.opExtrude","SWEPT_FACE",FACE,{"disambiguationData":[OSD([sQuery(id+"F7.wireOp",EDGE,"E60.right")])]});var subQ2=sQuery(id+"F5.wireOp",EDGE,"E57.top");Q8=makeQuery(id+"F13.boolean.opBoolean","SPLIT",EDGE,{"disambiguationData":[topologyDisambiguationEdgeConnected([makeQuery(id+"F13.opExtrude","SWEPT_FACE",FACE,{"disambiguationData":[OSD([subQ2])]})])],"derivedFrom":makeQuery(id+"F9.boolean.opBoolean","INTERSECT",EDGE,{"derivedFrom":[makeQuery(id+"F8.boolean.opBoolean","MERGE",FACE,{"derivedFrom":[subQ0,subQ1]}),makeQuery(id+"F9.opExtrude","SWEPT_FACE",FACE,{"disambiguationData":[OSD([subQ2])]})]})});}
            var Q9;
            Q9=makeQuery(id+"F9.boolean.opBoolean","INTERSECT",EDGE,{"derivedFrom":[makeQuery(id+"F8.boolean.opBoolean","COPY",FACE,{"derivedFrom":makeQuery(id+"F8.opExtrude","SWEPT_FACE",FACE,{"disambiguationData":[OSD([sQuery(id+"F7.wireOp",EDGE,"E60.top")])]})}),makeQuery(id+"F9.opExtrude","SWEPT_FACE",FACE,{"disambiguationData":[OSD([sQuery(id+"F5.wireOp",EDGE,"E57.top")])]})]});
            var Q10;
            Q10=makeQuery(id+"F9.boolean.opBoolean","INTERSECT",EDGE,{"derivedFrom":[makeQuery(id+"F8.boolean.opBoolean","COPY",FACE,{"derivedFrom":makeQuery(id+"F8.opExtrude","SWEPT_FACE",FACE,{"disambiguationData":[OSD([sQuery(id+"F7.wireOp",EDGE,"E60.top")])]})}),makeQuery(id+"F9.opExtrude","SWEPT_FACE",FACE,{"disambiguationData":[OSD([sQuery(id+"F5.wireOp",EDGE,"E58.top")])]})]});
            var Q11;
            {var subQ0=makeQuery(id+"F1.opExtrude","SWEPT_FACE",FACE,{"disambiguationData":[OSD([sQuery(id+"F0.wireOp",EDGE,"E2"),sQuery(id+"F0.wireOp",EDGE,"E23")])]});var subQ1=makeQuery(id+"F8.opExtrude","SWEPT_FACE",FACE,{"disambiguationData":[OSD([sQuery(id+"F7.wireOp",EDGE,"E60.left")])]});var subQ2=sQuery(id+"F5.wireOp",EDGE,"E58.top");Q11=makeQuery(id+"F13.boolean.opBoolean","SPLIT",EDGE,{"disambiguationData":[topologyDisambiguationEdgeConnected([makeQuery(id+"F13.opExtrude","SWEPT_FACE",FACE,{"disambiguationData":[OSD([subQ2])]})])],"derivedFrom":makeQuery(id+"F9.boolean.opBoolean","INTERSECT",EDGE,{"derivedFrom":[makeQuery(id+"F8.boolean.opBoolean","MERGE",FACE,{"derivedFrom":[subQ0,subQ1]}),makeQuery(id+"F9.opExtrude","SWEPT_FACE",FACE,{"disambiguationData":[OSD([subQ2])]})]})});}
            chamfer(context, id + "F15", {"entities" : qUnion([Q0, Q1, Q2, Q3, Q4, Q5, Q6, Q7, Q8, Q9, Q10, Q11]), "width" : 1 * mm});
        }
        {
            var Q0;
            {var subQ0=sQuery(id+"F5.wireOp",EDGE,"E58.top");Q0=makeQuery(id+"F13.boolean.opBoolean","SPLIT",EDGE,{"disambiguationData":[topologyDisambiguationEdgeConnected([makeQuery(id+"F13.opExtrude","SWEPT_FACE",FACE,{"disambiguationData":[OSD([subQ0])]})])],"derivedFrom":makeQuery(id+"F13.opExtrude","CAP_EDGE",EDGE,{"disambiguationData":[OSD([subQ0])],"isStart":false})});}
            var Q1;
            {var subQ0=sQuery(id+"F5.wireOp",EDGE,"E57.top");Q1=makeQuery(id+"F13.boolean.opBoolean","SPLIT",EDGE,{"disambiguationData":[topologyDisambiguationEdgeConnected([makeQuery(id+"F13.opExtrude","SWEPT_FACE",FACE,{"disambiguationData":[OSD([subQ0])]})])],"derivedFrom":makeQuery(id+"F13.opExtrude","CAP_EDGE",EDGE,{"disambiguationData":[OSD([subQ0])],"isStart":false})});}
            var Q2;
            {var subQ0=sQuery(id+"F5.wireOp",EDGE,"E56.top");Q2=makeQuery(id+"F13.boolean.opBoolean","SPLIT",EDGE,{"disambiguationData":[topologyDisambiguationEdgeConnected([makeQuery(id+"F13.opExtrude","SWEPT_FACE",FACE,{"disambiguationData":[OSD([subQ0])]})])],"derivedFrom":makeQuery(id+"F13.opExtrude","CAP_EDGE",EDGE,{"disambiguationData":[OSD([subQ0])],"isStart":false})});}
            var Q3;
            {var subQ0=sQuery(id+"F5.wireOp",EDGE,"E55.top");Q3=makeQuery(id+"F13.boolean.opBoolean","SPLIT",EDGE,{"disambiguationData":[topologyDisambiguationEdgeConnected([makeQuery(id+"F13.opExtrude","SWEPT_FACE",FACE,{"disambiguationData":[OSD([subQ0])]})])],"derivedFrom":makeQuery(id+"F13.opExtrude","CAP_EDGE",EDGE,{"disambiguationData":[OSD([subQ0])],"isStart":false})});}
            var Q4;
            {var subQ0=sQuery(id+"F5.wireOp",EDGE,"E54.bottom");Q4=makeQuery(id+"F13.boolean.opBoolean","SPLIT",EDGE,{"disambiguationData":[topologyDisambiguationEdgeConnected([makeQuery(id+"F13.opExtrude","SWEPT_FACE",FACE,{"disambiguationData":[OSD([subQ0])]})])],"derivedFrom":makeQuery(id+"F13.opExtrude","CAP_EDGE",EDGE,{"disambiguationData":[OSD([subQ0])],"isStart":false})});}
            var Q5;
            {var subQ0=sQuery(id+"F5.wireOp",EDGE,"E53.bottom");Q5=makeQuery(id+"F13.boolean.opBoolean","SPLIT",EDGE,{"disambiguationData":[topologyDisambiguationEdgeConnected([makeQuery(id+"F13.opExtrude","SWEPT_FACE",FACE,{"disambiguationData":[OSD([subQ0])]})])],"derivedFrom":makeQuery(id+"F13.opExtrude","CAP_EDGE",EDGE,{"disambiguationData":[OSD([subQ0])],"isStart":false})});}
            var Q6;
            Q6=makeQuery(id+"F13.opExtrude","CAP_EDGE",EDGE,{"disambiguationData":[OSD([sQuery(id+"F5.wireOp",EDGE,"E54.left")])],"isStart":false});
            var Q7;
            Q7=makeQuery(id+"F13.opExtrude","CAP_EDGE",EDGE,{"disambiguationData":[OSD([sQuery(id+"F5.wireOp",EDGE,"E55.right")])],"isStart":false});
            var Q8;
            Q8=makeQuery(id+"F13.opExtrude","CAP_EDGE",EDGE,{"disambiguationData":[OSD([sQuery(id+"F5.wireOp",EDGE,"E53.right")])],"isStart":false});
            var Q9;
            Q9=makeQuery(id+"F13.opExtrude","CAP_EDGE",EDGE,{"disambiguationData":[OSD([sQuery(id+"F5.wireOp",EDGE,"E56.left")])],"isStart":false});
            var Q10;
            Q10=makeQuery(id+"F13.opExtrude","CAP_EDGE",EDGE,{"disambiguationData":[OSD([sQuery(id+"F5.wireOp",EDGE,"E57.right")])],"isStart":false});
            var Q11;
            Q11=makeQuery(id+"F13.opExtrude","CAP_EDGE",EDGE,{"disambiguationData":[OSD([sQuery(id+"F5.wireOp",EDGE,"E58.left")])],"isStart":false});
            var Q12;
            Q12=makeQuery(id+"F13.opExtrude","CAP_EDGE",EDGE,{"disambiguationData":[OSD([sQuery(id+"F5.wireOp",EDGE,"E57.right")])],"isStart":true});
            var Q13;
            Q13=makeQuery(id+"F13.opExtrude","CAP_EDGE",EDGE,{"disambiguationData":[OSD([sQuery(id+"F5.wireOp",EDGE,"E56.left")])],"isStart":true});
            var Q14;
            Q14=makeQuery(id+"F13.opExtrude","CAP_EDGE",EDGE,{"disambiguationData":[OSD([sQuery(id+"F5.wireOp",EDGE,"E55.right")])],"isStart":true});
            var Q15;
            Q15=makeQuery(id+"F13.opExtrude","CAP_EDGE",EDGE,{"disambiguationData":[OSD([sQuery(id+"F5.wireOp",EDGE,"E54.left")])],"isStart":true});
            var Q16;
            Q16=makeQuery(id+"F13.opExtrude","CAP_EDGE",EDGE,{"disambiguationData":[OSD([sQuery(id+"F5.wireOp",EDGE,"E53.right")])],"isStart":true});
            var Q17;
            Q17=makeQuery(id+"F13.opExtrude","CAP_EDGE",EDGE,{"disambiguationData":[OSD([sQuery(id+"F5.wireOp",EDGE,"E58.left")])],"isStart":true});
            var Q18;
            {var subQ0=sQuery(id+"F0.wireOp",EDGE,"E30");var subQ1=sQuery(id+"F0.wireOp",EDGE,"E1");Q18=makeQuery(id+"F6.opChamfer","BLEND_EDGE",EDGE,{"blendedFrom":[makeQuery(id+"F1.opExtrude","CAP_EDGE",EDGE,{"disambiguationData":[OSD([subQ1]),TDD([makeQuery(id+"F0.imprint","IMPRINT",EDGE,{"disambiguationData":[TD([[makeQuery(id+"F0.imprint","INTERSECT",VERTEX,{"derivedFrom":[subQ1,sQuery(id+"F0.wireOp",EDGE,"E4")]}),1.0]])],"derivedFrom":subQ1})])],"isStart":false}),makeQuery(id+"F2.boolean.opBoolean","MERGE",FACE,{"derivedFrom":[makeQuery(id+"F1.opExtrude","SWEPT_FACE",FACE,{"disambiguationData":[OSD([subQ0])]}),makeQuery(id+"F2.opExtrude","SWEPT_FACE",FACE,{"disambiguationData":[OSD([sQuery(id+"F0.wireOp",EDGE,"E46.left")])]})]})],"blendedInto":[makeQuery(id+"F2.boolean.opBoolean","MERGE",FACE,{"derivedFrom":[makeQuery(id+"F1.opExtrude","SWEPT_FACE",FACE,{"disambiguationData":[OSD([subQ0])]}),makeQuery(id+"F2.opExtrude","SWEPT_FACE",FACE,{"disambiguationData":[OSD([sQuery(id+"F0.wireOp",EDGE,"E46.left")])]})]})]});}
            var Q19;
            {var subQ0=sQuery(id+"F0.wireOp",EDGE,"E32");var subQ1=sQuery(id+"F0.wireOp",EDGE,"E1");Q19=makeQuery(id+"F6.opChamfer","BLEND_EDGE",EDGE,{"blendedFrom":[makeQuery(id+"F1.opExtrude","CAP_EDGE",EDGE,{"disambiguationData":[OSD([subQ1]),TDD([makeQuery(id+"F0.imprint","IMPRINT",EDGE,{"disambiguationData":[TD([[makeQuery(id+"F0.imprint","INTERSECT",VERTEX,{"derivedFrom":[subQ1,sQuery(id+"F0.wireOp",EDGE,"E17")]}),-1.0]])],"derivedFrom":subQ1})])],"isStart":false}),makeQuery(id+"F2.boolean.opBoolean","MERGE",FACE,{"derivedFrom":[makeQuery(id+"F1.opExtrude","SWEPT_FACE",FACE,{"disambiguationData":[OSD([subQ0])]}),makeQuery(id+"F2.opExtrude","SWEPT_FACE",FACE,{"disambiguationData":[OSD([sQuery(id+"F0.wireOp",EDGE,"E49.right")])]})]})],"blendedInto":[makeQuery(id+"F2.boolean.opBoolean","MERGE",FACE,{"derivedFrom":[makeQuery(id+"F1.opExtrude","SWEPT_FACE",FACE,{"disambiguationData":[OSD([subQ0])]}),makeQuery(id+"F2.opExtrude","SWEPT_FACE",FACE,{"disambiguationData":[OSD([sQuery(id+"F0.wireOp",EDGE,"E49.right")])]})]})]});}
            var Q20;
            Q20=makeQuery(id+"F12.boolean.opBoolean","COPY",EDGE,{"derivedFrom":makeQuery(id+"F12.opExtrude","SWEPT_EDGE",EDGE,{"disambiguationData":[OSD([sQuery(id+"F5.wireOp",EDGE,"E53.bottom"),sQuery(id+"F10.wireOp",EDGE,"E63")])]})});
            var Q21;
            Q21=makeQuery(id+"F12.boolean.opBoolean","COPY",EDGE,{"derivedFrom":makeQuery(id+"F12.opExtrude","SWEPT_EDGE",EDGE,{"disambiguationData":[OSD([sQuery(id+"F5.wireOp",EDGE,"E54.bottom"),sQuery(id+"F10.wireOp",EDGE,"E63")])]})});
            var Q22;
            Q22=makeQuery(id+"F9.boolean.opBoolean","COPY",EDGE,{"derivedFrom":makeQuery(id+"F9.opExtrude","SWEPT_EDGE",EDGE,{"disambiguationData":[OSD([sQuery(id+"F5.wireOp",EDGE,"E56.top"),sQuery(id+"F5.wireOp",EDGE,"E59")])]})});
            var Q23;
            Q23=makeQuery(id+"F9.boolean.opBoolean","COPY",EDGE,{"derivedFrom":makeQuery(id+"F9.opExtrude","SWEPT_EDGE",EDGE,{"disambiguationData":[OSD([sQuery(id+"F5.wireOp",EDGE,"E55.top"),sQuery(id+"F5.wireOp",EDGE,"E59")])]})});
            var Q24;
            Q24=makeQuery(id+"F12.boolean.opBoolean","COPY",EDGE,{"derivedFrom":makeQuery(id+"F12.opExtrude","SWEPT_EDGE",EDGE,{"disambiguationData":[OSD([sQuery(id+"F5.wireOp",EDGE,"E57.top"),sQuery(id+"F11.wireOp",EDGE,"E64")])]})});
            var Q25;
            Q25=makeQuery(id+"F12.boolean.opBoolean","COPY",EDGE,{"derivedFrom":makeQuery(id+"F12.opExtrude","SWEPT_EDGE",EDGE,{"disambiguationData":[OSD([sQuery(id+"F5.wireOp",EDGE,"E58.top"),sQuery(id+"F11.wireOp",EDGE,"E64")])]})});
            var Q26;
            Q26=makeQuery(id+"F3.opExtrude","SWEPT_EDGE",EDGE,{"disambiguationData":[OSD([sQuery(id+"F0.wireOp",EDGE,"E41"),sQuery(id+"F0.wireOp",EDGE,"E42"),sQuery(id+"F0.wireOp",EDGE,"E52")])]});
            var Q27;
            Q27=makeQuery(id+"F3.opExtrude","SWEPT_EDGE",EDGE,{"disambiguationData":[OSD([sQuery(id+"F0.wireOp",EDGE,"E39"),sQuery(id+"F0.wireOp",EDGE,"E40"),sQuery(id+"F0.wireOp",EDGE,"E51")])]});
            var Q28;
            Q28=makeQuery(id+"F3.opExtrude","SWEPT_EDGE",EDGE,{"disambiguationData":[OSD([sQuery(id+"F0.wireOp",EDGE,"E43"),sQuery(id+"F0.wireOp",EDGE,"E44"),sQuery(id+"F0.wireOp",EDGE,"E52")])]});
            var Q29;
            Q29=makeQuery(id+"F3.opExtrude","CAP_EDGE",EDGE,{"disambiguationData":[OSD([sQuery(id+"F0.wireOp",EDGE,"E43")])],"isStart":false});
            var Q30;
            Q30=makeQuery(id+"F3.opExtrude","CAP_EDGE",EDGE,{"disambiguationData":[OSD([sQuery(id+"F0.wireOp",EDGE,"E41")])],"isStart":false});
            var Q31;
            Q31=makeQuery(id+"F3.opExtrude","CAP_EDGE",EDGE,{"disambiguationData":[OSD([sQuery(id+"F0.wireOp",EDGE,"E39")])],"isStart":false});
            var Q32;
            Q32=makeQuery(id+"F3.opExtrude","SWEPT_EDGE",EDGE,{"disambiguationData":[OSD([sQuery(id+"F0.wireOp",EDGE,"E37"),sQuery(id+"F0.wireOp",EDGE,"E38"),sQuery(id+"F0.wireOp",EDGE,"E51")])]});
            var Q33;
            Q33=makeQuery(id+"F3.opExtrude","CAP_EDGE",EDGE,{"disambiguationData":[OSD([sQuery(id+"F0.wireOp",EDGE,"E37")])],"isStart":false});
            var Q34;
            Q34=makeQuery(id+"F3.opExtrude","SWEPT_EDGE",EDGE,{"disambiguationData":[OSD([sQuery(id+"F0.wireOp",EDGE,"E35"),sQuery(id+"F0.wireOp",EDGE,"E36"),sQuery(id+"F0.wireOp",EDGE,"E50")])]});
            var Q35;
            Q35=makeQuery(id+"F3.opExtrude","CAP_EDGE",EDGE,{"disambiguationData":[OSD([sQuery(id+"F0.wireOp",EDGE,"E35")])],"isStart":false});
            var Q36;
            Q36=makeQuery(id+"F3.opExtrude","SWEPT_EDGE",EDGE,{"disambiguationData":[OSD([sQuery(id+"F0.wireOp",EDGE,"E33"),sQuery(id+"F0.wireOp",EDGE,"E34"),sQuery(id+"F0.wireOp",EDGE,"E50")])]});
            var Q37;
            Q37=makeQuery(id+"F3.opExtrude","CAP_EDGE",EDGE,{"disambiguationData":[OSD([sQuery(id+"F0.wireOp",EDGE,"E33")])],"isStart":false});
            var Q38;
            Q38=makeQuery(id+"F3.opExtrude","SWEPT_EDGE",EDGE,{"disambiguationData":[OSD([sQuery(id+"F0.wireOp",EDGE,"E1"),sQuery(id+"F0.wireOp",EDGE,"E34")])]});
            var Q39;
            Q39=makeQuery(id+"F3.opExtrude","CAP_EDGE",EDGE,{"disambiguationData":[OSD([sQuery(id+"F0.wireOp",EDGE,"E34")])],"isStart":false});
            var Q40;
            Q40=makeQuery(id+"F3.opExtrude","CAP_EDGE",EDGE,{"disambiguationData":[OSD([sQuery(id+"F0.wireOp",EDGE,"E36")])],"isStart":false});
            var Q41;
            Q41=makeQuery(id+"F3.opExtrude","SWEPT_EDGE",EDGE,{"disambiguationData":[OSD([sQuery(id+"F0.wireOp",EDGE,"E1"),sQuery(id+"F0.wireOp",EDGE,"E36")])]});
            var Q42;
            Q42=makeQuery(id+"F3.opExtrude","CAP_EDGE",EDGE,{"disambiguationData":[OSD([sQuery(id+"F0.wireOp",EDGE,"E38")])],"isStart":false});
            var Q43;
            Q43=makeQuery(id+"F3.opExtrude","SWEPT_EDGE",EDGE,{"disambiguationData":[OSD([sQuery(id+"F0.wireOp",EDGE,"E1"),sQuery(id+"F0.wireOp",EDGE,"E38")])]});
            var Q44;
            Q44=makeQuery(id+"F3.opExtrude","CAP_EDGE",EDGE,{"disambiguationData":[OSD([sQuery(id+"F0.wireOp",EDGE,"E40")])],"isStart":false});
            var Q45;
            Q45=makeQuery(id+"F3.opExtrude","CAP_EDGE",EDGE,{"disambiguationData":[OSD([sQuery(id+"F0.wireOp",EDGE,"E42")])],"isStart":false});
            var Q46;
            Q46=makeQuery(id+"F3.opExtrude","SWEPT_EDGE",EDGE,{"disambiguationData":[OSD([sQuery(id+"F0.wireOp",EDGE,"E1"),sQuery(id+"F0.wireOp",EDGE,"E40")])]});
            var Q47;
            Q47=makeQuery(id+"F3.opExtrude","SWEPT_EDGE",EDGE,{"disambiguationData":[OSD([sQuery(id+"F0.wireOp",EDGE,"E1"),sQuery(id+"F0.wireOp",EDGE,"E42")])]});
            var Q48;
            Q48=makeQuery(id+"F3.opExtrude","CAP_EDGE",EDGE,{"disambiguationData":[OSD([sQuery(id+"F0.wireOp",EDGE,"E44")])],"isStart":false});
            var Q49;
            Q49=makeQuery(id+"F3.opExtrude","SWEPT_EDGE",EDGE,{"disambiguationData":[OSD([sQuery(id+"F0.wireOp",EDGE,"E1"),sQuery(id+"F0.wireOp",EDGE,"E44")])]});
            var Q50;
            {var subQ0=sQuery(id+"F0.wireOp",EDGE,"E1");var subQ1=makeQuery(id+"F0.imprint","INTERSECT",VERTEX,{"derivedFrom":[subQ0,sQuery(id+"F0.wireOp",EDGE,"E17")]});Q50=makeQuery(id+"F3.boolean.opBoolean","MERGE",EDGE,{"derivedFrom":[makeQuery(id+"F1.opExtrude","CAP_EDGE",EDGE,{"disambiguationData":[OSD([subQ0]),TDD([makeQuery(id+"F0.imprint","IMPRINT",EDGE,{"disambiguationData":[TD([[subQ1,-1.0]])],"derivedFrom":subQ0})])],"isStart":true}),makeQuery(id+"F3.opExtrude","CAP_EDGE",EDGE,{"disambiguationData":[OSD([subQ0]),TDD([makeQuery(id+"F0.imprint","IMPRINT",EDGE,{"disambiguationData":[TD([[subQ1,1.0]])],"derivedFrom":subQ0})])],"isStart":true})]});}
            var Q51;
            {var subQ0=sQuery(id+"F0.wireOp",EDGE,"E1");var subQ1=makeQuery(id+"F0.imprint","INTERSECT",VERTEX,{"derivedFrom":[subQ0,sQuery(id+"F0.wireOp",EDGE,"E14")]});var subQ2=makeQuery(id+"F0.imprint","INTERSECT",VERTEX,{"derivedFrom":[subQ0,sQuery(id+"F0.wireOp",EDGE,"E11")]});Q51=makeQuery(id+"F3.boolean.opBoolean","MERGE",EDGE,{"derivedFrom":[makeQuery(id+"F1.opExtrude","CAP_EDGE",EDGE,{"disambiguationData":[OSD([subQ0]),TDD([makeQuery(id+"F0.imprint","IMPRINT",EDGE,{"disambiguationData":[TD([[subQ2,-1.0]])],"derivedFrom":subQ0})])],"isStart":true}),makeQuery(id+"F3.opExtrude","CAP_EDGE",EDGE,{"disambiguationData":[OSD([subQ0]),TDD([makeQuery(id+"F0.imprint","IMPRINT",EDGE,{"disambiguationData":[TD([[subQ2,1.0]])],"derivedFrom":subQ0})])],"isStart":true}),makeQuery(id+"F3.opExtrude","CAP_EDGE",EDGE,{"disambiguationData":[OSD([subQ0]),TDD([makeQuery(id+"F0.imprint","IMPRINT",EDGE,{"disambiguationData":[TD([[subQ1,-1.0]])],"derivedFrom":subQ0})])],"isStart":true})]});}
            var Q52;
            {var subQ0=sQuery(id+"F0.wireOp",EDGE,"E1");var subQ1=makeQuery(id+"F0.imprint","INTERSECT",VERTEX,{"derivedFrom":[subQ0,sQuery(id+"F0.wireOp",EDGE,"E8")]});var subQ2=makeQuery(id+"F0.imprint","INTERSECT",VERTEX,{"derivedFrom":[subQ0,sQuery(id+"F0.wireOp",EDGE,"E6")]});Q52=makeQuery(id+"F3.boolean.opBoolean","MERGE",EDGE,{"derivedFrom":[makeQuery(id+"F1.opExtrude","CAP_EDGE",EDGE,{"disambiguationData":[OSD([subQ0]),TDD([makeQuery(id+"F0.imprint","IMPRINT",EDGE,{"disambiguationData":[TD([[subQ2,-1.0]])],"derivedFrom":subQ0})])],"isStart":true}),makeQuery(id+"F3.opExtrude","CAP_EDGE",EDGE,{"disambiguationData":[OSD([subQ0]),TDD([makeQuery(id+"F0.imprint","IMPRINT",EDGE,{"disambiguationData":[TD([[subQ2,1.0]])],"derivedFrom":subQ0})])],"isStart":true}),makeQuery(id+"F3.opExtrude","CAP_EDGE",EDGE,{"disambiguationData":[OSD([subQ0]),TDD([makeQuery(id+"F0.imprint","IMPRINT",EDGE,{"disambiguationData":[TD([[subQ1,-1.0]])],"derivedFrom":subQ0})])],"isStart":true})]});}
            var Q53;
            {var subQ0=sQuery(id+"F0.wireOp",EDGE,"E1");var subQ1=makeQuery(id+"F0.imprint","INTERSECT",VERTEX,{"derivedFrom":[subQ0,sQuery(id+"F0.wireOp",EDGE,"E4")]});Q53=makeQuery(id+"F3.boolean.opBoolean","MERGE",EDGE,{"derivedFrom":[makeQuery(id+"F1.opExtrude","CAP_EDGE",EDGE,{"disambiguationData":[OSD([subQ0]),TDD([makeQuery(id+"F0.imprint","IMPRINT",EDGE,{"disambiguationData":[TD([[subQ1,1.0]])],"derivedFrom":subQ0})])],"isStart":true}),makeQuery(id+"F3.opExtrude","CAP_EDGE",EDGE,{"disambiguationData":[OSD([subQ0]),TDD([makeQuery(id+"F0.imprint","IMPRINT",EDGE,{"disambiguationData":[TD([[subQ1,-1.0]])],"derivedFrom":subQ0})])],"isStart":true})]});}
            fillet(context, id + "F16", {"entities" : qUnion([Q0, Q1, Q2, Q3, Q4, Q5, Q6, Q7, Q8, Q9, Q10, Q11, Q12, Q13, Q14, Q15, Q16, Q17, Q18, Q19, Q20, Q21, Q22, Q23, Q24, Q25, Q26, Q27, Q28, Q29, Q30, Q31, Q32, Q33, Q34, Q35, Q36, Q37, Q38, Q39, Q40, Q41, Q42, Q43, Q44, Q45, Q46, Q47, Q48, Q49, Q50, Q51, Q52, Q53]), "radius" : 1 * mm, "tangentPropagation" : true, "allowEdgeOverflow" : false});
        }
    });
